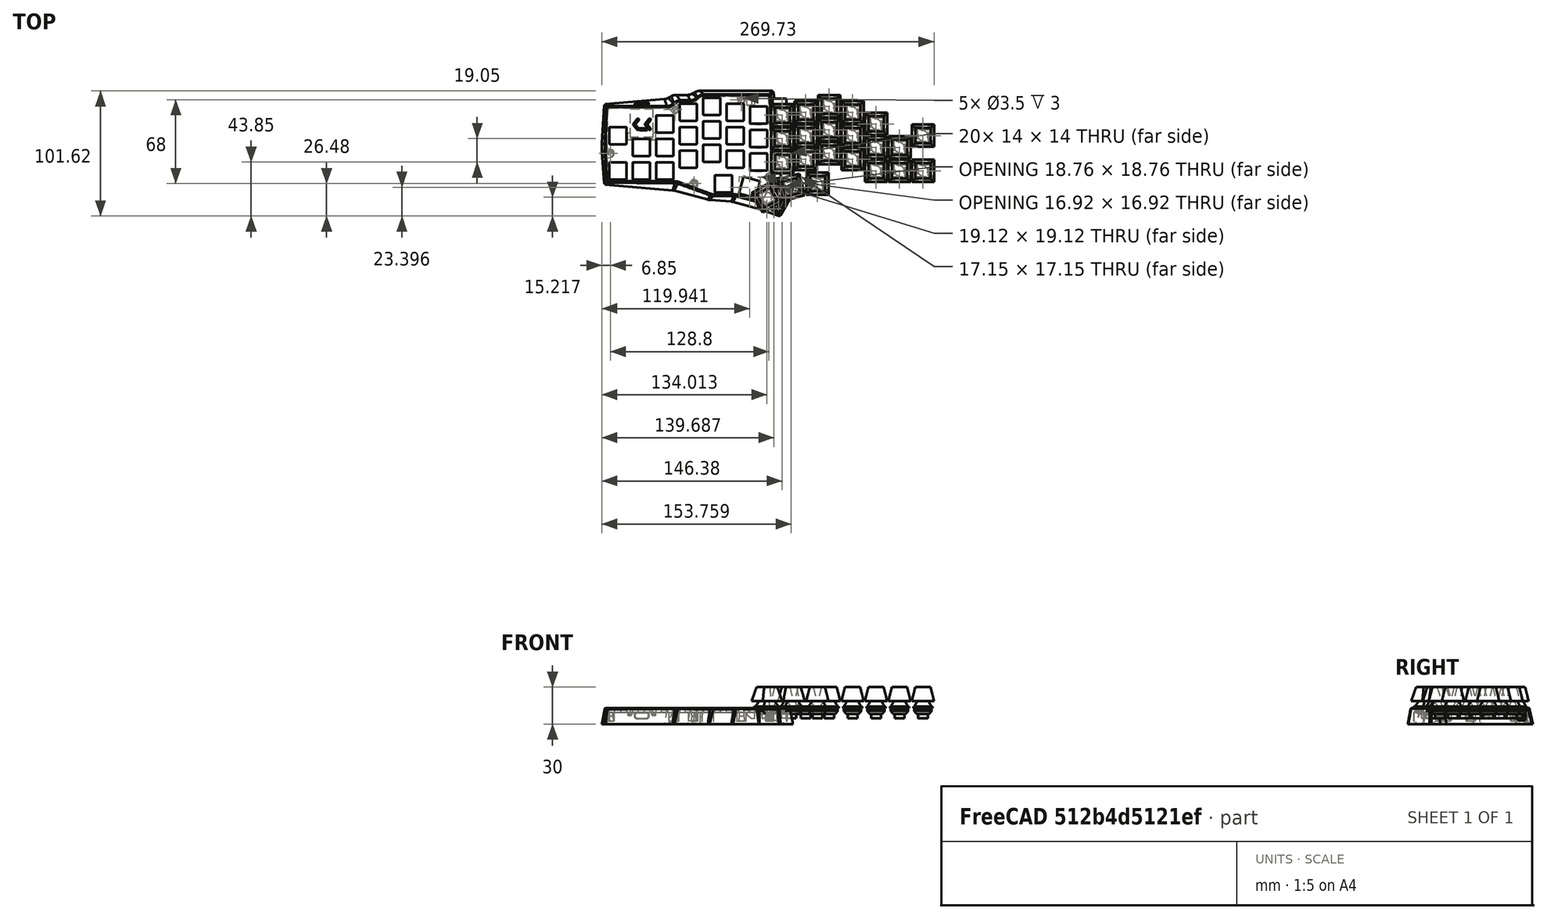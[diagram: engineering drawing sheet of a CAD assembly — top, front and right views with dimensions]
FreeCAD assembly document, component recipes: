
FREECAD ASSEMBLY — COMPONENT RECIPES ("plate6")

This assembly document has 8 components, labeled P0..P7 below (a component is one placed body or linked part). 8 of them carry a construction recipe — the FreeCAD feature program that regenerates the part from scratch, quoted from this document or its linked companion documents; the rest are supplied as boundary geometry only. No exploded tour is included for this assembly.
COMPONENT P0 — recipe-attached ("CaseSolid", modeled in this document).
Construction recipe (the document's own serialized feature program — sketch geometry with constraints, then the solid features built on it; lengths are millimeters unless a unit is written):

FEATURE [PartDesign::ShapeBinder] ShapeBinder
  Support = -> [Compound]
  TraceSupport = false
FEATURE [Sketcher::SketchObject] Sketch  label="SketchTop"
  ExternalGeometry = -> [ShapeBinder]
  FullyConstrained = true
  MapMode = 5
  Support = -> [XY_Plane]
  sketch-geometry (19):
    g0: LineSegment StartX=57.15 StartY=7.14375 StartZ=0 EndX=61.9125 EndY=2.38125 EndZ=0
    g1: LineSegment StartX=61.9125 StartY=2.38125 StartZ=0 EndX=76.2 EndY=2.38125 EndZ=0
    g2: LineSegment StartX=76.2 StartY=2.38125 StartZ=0 EndX=80.9625 EndY=-2.38124 EndZ=0
    g3: LineSegment StartX=80.9625 StartY=-2.38124 StartZ=0 EndX=133.35 EndY=-2.38124 EndZ=0
    g4: LineSegment StartX=133.35 StartY=-2.38124 StartZ=0 EndX=134.35 EndY=-33.2188 EndZ=0
    g5: LineSegment StartX=134.35 StartY=-38.2188 StartZ=0 EndX=133.35 EndY=-64.2937 EndZ=0
    g6: LineSegment StartX=133.35 StartY=-64.2937 StartZ=0 EndX=76.2 EndY=-64.2937 EndZ=0
    g7: LineSegment StartX=76.2 StartY=-64.2937 StartZ=0 EndX=47.625 EndY=-74.8187 EndZ=0
    g8: LineSegment StartX=47.625 StartY=-74.8187 StartZ=0 EndX=28.575 EndY=-74.8187 EndZ=0
    g9: LineSegment StartX=28.575 StartY=-74.8187 StartZ=0 EndX=10.1741 EndY=-79.7492 EndZ=0
    g10: LineSegment StartX=10.1741 StartY=-79.7492 StartZ=0 EndX=-6.75668 EndY=-89.5242 EndZ=0
    g11: LineSegment StartX=-16.2817 StartY=-73.0265 StartZ=0 EndX=-3.16979 EndY=-65.4563 EndZ=0
    g12: LineSegment StartX=-3.16979 StartY=-65.4563 StartZ=0 EndX=-4e-16 EndY=7.14375 EndZ=0
    g13: LineSegment StartX=-4e-16 StartY=7.14375 StartZ=0 EndX=57.15 EndY=7.14375 EndZ=0
    g14: LineSegment StartX=134.35 StartY=-33.2188 StartZ=0 EndX=134.35 EndY=-35.7188 EndZ=0
    g15: LineSegment StartX=134.35 StartY=-35.7188 StartZ=0 EndX=134.35 EndY=-38.2188 EndZ=0
    g16: GeomPoint X=133.35 Y=-7.14393 Z=0
    g17: GeomPoint X=133.35 Y=-35.7188 Z=0
    g18: LineSegment StartX=-16.2817 StartY=-73.0265 StartZ=0 EndX=-6.75668 EndY=-89.5242 EndZ=0
  constraints (47):
    c: Coincident(g0,g1)
    c: Horizontal(g1)
    c: Coincident(g1,g2)
    c: Coincident(g2,g3)
    c: Horizontal(g3)
    c: Coincident(g3,g4)
    c: Coincident(g5,g6)
    c: Horizontal(g6)
    c: Coincident(g6,g7)
    c: Coincident(g7,g8)
    c: Coincident(g8,g9)
    c: Coincident(g9,g10)
    c: Coincident(g11,g12)
    c: Coincident(g12,g13)
    c: Horizontal(g13)
    c: Coincident(g13,g0)
    c: Coincident(g-4,g0)
    c: Coincident(g1,g-5)
    c: Angle(g13,g0) = 2.35619
    c: Equal(g0,g2)
    c: Angle(g1,g2) = 2.35619
    c: Vertical(g-1,g12)
    c: Angle(g12,g13) = 1.61443
    c: Parallel(g-12,g11)
    c: Coincident(g9,g-13)
    c: Coincident(g-14,g8)
    c: Coincident(g7,g-14)
    c: Coincident(g5,g-8)
    c: Coincident(g4,g14)
    c: Vertical(g14)
    c: Coincident(g14,g15)
    c: Coincident(g15,g5)
    c: Vertical(g15)
    c: Equal(g15,g14)
    c: Coincident(g16,g-7)
    c: Symmetric(g16,g5,g17)
    c: Horizontal(g17,g14)
    c: DistanceX(g17,g14) = 1
    c: DistanceY(g14,g14) = 2.5
    c: Vertical(g3,g5)
    c: Vertical(g-9,g6)
    c: Parallel(g-10,g10)
    c: Coincident(g18,g11)
    c: Coincident(g18,g10)
    c: Parallel(g18,g-11)
    c: Distance(g-12,g18) = 0.5
    c: PointOnObject(g11,g-12)
FEATURE [Sketcher::SketchObject] Sketch001  label="SketchBot"
  AttachmentOffset = pos=(0,0,-13) rot=(0,0,1;0rad)
  ExternalGeometry = -> [ShapeBinder]
  FullyConstrained = true
  MapMode = 5
  Placement = pos=(0,0,-13) rot=(0,0,1;0rad)
  Support = -> [XY_Plane]
  expr: .AttachmentOffset.Base.z = 0 mm - <<S>>.caseHeight
  sketch-geometry (18):
    g0: LineSegment StartX=59.65 StartY=10.1437 StartZ=0 EndX=65.3008 EndY=6.88125 EndZ=0
    g1: LineSegment StartX=65.3008 StartY=6.88125 StartZ=0 EndX=78.7 EndY=6.88125 EndZ=0
    g2: LineSegment StartX=78.7 StartY=6.88125 StartZ=0 EndX=84.3508 EndY=3.61876 EndZ=0
    g3: LineSegment StartX=84.3508 StartY=3.61876 StartZ=0 EndX=134.929 EndY=-0.806253 EndZ=0
    g4: LineSegment StartX=134.929 StartY=-0.806253 StartZ=0 EndX=136.85 EndY=-32.2188 EndZ=0
    g5: LineSegment StartX=136.85 StartY=-32.2188 StartZ=0 EndX=136.85 EndY=-35.7188 EndZ=0
    g6: LineSegment StartX=136.85 StartY=-35.7188 StartZ=0 EndX=136.85 EndY=-39.2188 EndZ=0
    g7: LineSegment StartX=136.85 StartY=-39.2188 StartZ=0 EndX=134.929 EndY=-65.7937 EndZ=0
    g8: LineSegment StartX=78.7 StartY=-70.7131 StartZ=0 EndX=50.125 EndY=-78.3698 EndZ=0
    g9: LineSegment StartX=50.125 StartY=-78.3698 StartZ=0 EndX=31.075 EndY=-79.7992 EndZ=0
    g10: LineSegment StartX=31.075 StartY=-79.7992 StartZ=0 EndX=9.17411 EndY=-85.6675 EndZ=0
    g11: LineSegment StartX=9.17411 StartY=-85.6675 StartZ=0 EndX=-7.73873 EndY=-91.8233 EndZ=0
    g12: LineSegment StartX=-7.73873 StartY=-91.8233 StartZ=0 EndX=-18.7637 EndY=-72.7274 EndZ=0
    g13: LineSegment StartX=-18.7637 StartY=-72.7274 StartZ=0 EndX=-8.88611 EndY=-62.8498 EndZ=0
    g14: LineSegment StartX=-8.88611 StartY=-62.8498 StartZ=0 EndX=-2.5 EndY=10.1437 EndZ=0
    g15: LineSegment StartX=-2.5 StartY=10.1437 StartZ=0 EndX=59.65 EndY=10.1437 EndZ=0
    g16: GeomPoint X=133.35 Y=-35.7188 Z=0
    g17: LineSegment StartX=78.7 StartY=-70.7131 StartZ=0 EndX=134.929 EndY=-65.7937 EndZ=0
  constraints (52):
    c: Coincident(g0,g1)
    c: Horizontal(g1)
    c: Coincident(g1,g2)
    c: Coincident(g2,g3)
    c: Coincident(g3,g4)
    c: Coincident(g4,g5)
    c: Coincident(g5,g6)
    c: Coincident(g6,g7)
    c: Coincident(g8,g9)
    c: Coincident(g9,g10)
    c: Coincident(g10,g11)
    c: Coincident(g11,g12)
    c: Coincident(g12,g13)
    c: Coincident(g13,g14)
    c: Coincident(g14,g15)
    c: Horizontal(g15)
    c: DistanceY(g-4,g15) = 3
    c: DistanceX(g-4,g15) = 2.5
    c: Coincident(g0,g15)
    c: DistanceY(g-5,g1) = 4.5
    c: DistanceX(g-5,g1) = 2.5
    c: Angle(g15,g0) = 2.61799
    c: Equal(g0,g2)
    c: Angle(g1,g2) = 2.61799
    c: Vertical(g5)
    c: Vertical(g6)
    c: Symmetric(g-7,g-8,g16)
    c: Horizontal(g16,g5)
    c: DistanceX(g16,g5) = 3.5
    c: DistanceY(g5,g5) = 3.5
    c: Equal(g5,g6)
    c: Vertical(g7,g3)
    c: Parallel(g12,g-11)
    c: Angle(g12,g13) = 1.8326
    c: Angle(g11,g12) = 1.74533
    c: Distance(g-11,g12) = 2.5
    c: Distance(g12,g-10) = 1.5
    c: Distance(g11,g-12) = 1.5
    c: Angle(g14,g15) = 1.65806
    c: DistanceX(g14,g-1) = 2.5
    c: DistanceY(g7,g-8) = 1.5
    c: DistanceX(g-9,g8) = 2.5
    c: Parallel(g-13,g10)
    c: DistanceX(g-14,g8) = 2.5
    c: DistanceX(g-14,g9) = 2.5
    c: DistanceX(g10,g-13) = 1
    c: Angle(g-2,g4) = 0.0610865
    c: Angle(g-1,g3) = 3.05433
    c: Coincident(g17,g8)
    c: Coincident(g17,g7)
    c: Angle(g-1,g17) = 0.0872665
    c: Angle(g8,g17) = 2.96706
FEATURE [Sketcher::SketchObject] Sketch002
  AttachmentOffset = pos=(0,0,-3.6) rot=(0,0,1;0rad)
  ExternalGeometry = -> [Sketch]
  FullyConstrained = false
  MapMode = 5
  Placement = pos=(0,0,-3.6) rot=(0,0,1;0rad)
  Support = -> [XY_Plane]
  expr: .AttachmentOffset.Base.z = -<<S>>.topThk
  sketch-geometry (17):
    g0: LineSegment StartX=1.43594 StartY=5.64375 StartZ=0 EndX=56.5287 EndY=5.64375 EndZ=0
    g1: LineSegment StartX=56.5287 StartY=5.64375 StartZ=0 EndX=61.2912 EndY=0.881255 EndZ=0
    g2: LineSegment StartX=61.2912 StartY=0.881255 StartZ=0 EndX=75.5787 EndY=0.881255 EndZ=0
    g3: LineSegment StartX=75.5787 StartY=0.881255 StartZ=0 EndX=80.3412 EndY=-3.88124 EndZ=0
    g4: LineSegment StartX=80.3412 StartY=-3.88124 StartZ=0 EndX=131.898 EndY=-3.88124 EndZ=0
    g5: LineSegment StartX=131.898 StartY=-3.88124 StartZ=0 EndX=132.851 EndY=-33.2719 EndZ=0
    g6: LineSegment StartX=132.851 StartY=-33.2719 StartZ=0 EndX=132.851 EndY=-35.7188 EndZ=0
    g7: LineSegment StartX=132.851 StartY=-35.7188 StartZ=0 EndX=132.851 EndY=-38.1658 EndZ=0
    g8: LineSegment StartX=132.851 StartY=-38.1658 StartZ=0 EndX=131.906 EndY=-62.7937 EndZ=0
    g9: LineSegment StartX=131.906 StartY=-62.7937 StartZ=0 EndX=75.9325 EndY=-62.7937 EndZ=0
    g10: LineSegment StartX=75.9325 StartY=-62.7937 StartZ=0 EndX=47.3575 EndY=-73.3187 EndZ=0
    g11: LineSegment StartX=47.3575 StartY=-73.3187 StartZ=0 EndX=28.3775 EndY=-73.3187 EndZ=0
    g12: LineSegment StartX=28.3775 StartY=-73.3187 StartZ=0 EndX=9.59513 EndY=-78.3515 EndZ=0
    g13: LineSegment StartX=9.59513 StartY=-78.3515 StartZ=0 EndX=-5.77463 EndY=-87.2252 EndZ=0
    g14: LineSegment StartX=-5.77463 StartY=-87.2252 StartZ=0 EndX=-13.7996 EndY=-73.3255 EndZ=0
    g15: LineSegment StartX=-13.7996 StartY=-73.3255 StartZ=0 EndX=-1.70711 EndY=-66.3439 EndZ=0
    g16: LineSegment StartX=-1.70711 StartY=-66.3439 StartZ=0 EndX=1.43594 EndY=5.64375 EndZ=0
  constraints (24):
    c: Horizontal(g0)
    c: Coincident(g0,g1)
    c: Coincident(g1,g2)
    c: Horizontal(g2)
    c: Coincident(g2,g3)
    c: Coincident(g3,g4)
    c: Horizontal(g4)
    c: Coincident(g4,g5)
    c: Coincident(g5,g6)
    c: Vertical(g6)
    c: Coincident(g6,g7)
    c: Vertical(g7)
    c: Coincident(g7,g8)
    c: Coincident(g8,g9)
    c: Horizontal(g9)
    c: Coincident(g9,g10)
    c: Coincident(g10,g11)
    c: Coincident(g11,g12)
    c: Coincident(g12,g13)
    c: Coincident(g13,g14)
    c: Coincident(g14,g15)
    c: Coincident(g15,g16)
    c: Coincident(g16,g0)
    c: Equal(g6,g7)
FEATURE [Sketcher::SketchObject] Sketch003
  AttachmentOffset = pos=(0,0,-3) rot=(0,0,1;0rad)
  FullyConstrained = true
  MapMode = 5
  Placement = pos=(0,0,-3) rot=(0,0,1;0rad)
  Support = -> [XY_Plane]
  expr: .AttachmentOffset.Base.z = -3
  sketch-geometry (12):
    g0: LineSegment StartX=115.875 StartY=-23.625 StartZ=0 EndX=113.875 EndY=-23.625 EndZ=0
    g1: LineSegment StartX=113.875 StartY=-23.625 StartZ=0 EndX=113.875 EndY=-27.625 EndZ=0
    g2: LineSegment StartX=113.875 StartY=-27.625 StartZ=0 EndX=112.375 EndY=-27.625 EndZ=0
    g3: LineSegment StartX=112.375 StartY=-27.625 StartZ=0 EndX=112.375 EndY=-29.625 EndZ=0
    g4: LineSegment StartX=112.375 StartY=-29.625 StartZ=0 EndX=115.875 EndY=-29.625 EndZ=0
    g5: LineSegment StartX=115.875 StartY=-29.625 StartZ=0 EndX=115.875 EndY=-23.625 EndZ=0
    g6: LineSegment StartX=95.275 StartY=-23.625 StartZ=0 EndX=93.275 EndY=-23.625 EndZ=0
    g7: LineSegment StartX=93.275 StartY=-23.625 StartZ=0 EndX=93.275 EndY=-29.625 EndZ=0
    g8: LineSegment StartX=93.275 StartY=-29.625 StartZ=0 EndX=96.775 EndY=-29.625 EndZ=0
    g9: LineSegment StartX=96.775 StartY=-29.625 StartZ=0 EndX=96.775 EndY=-27.625 EndZ=0
    g10: LineSegment StartX=96.775 StartY=-27.625 StartZ=0 EndX=95.275 EndY=-27.625 EndZ=0
    g11: LineSegment StartX=95.275 StartY=-27.625 StartZ=0 EndX=95.275 EndY=-23.625 EndZ=0
  constraints (36):
    c: Horizontal(g0)
    c: Coincident(g0,g1)
    c: Coincident(g1,g2)
    c: Coincident(g2,g3)
    c: Coincident(g3,g4)
    c: Horizontal(g4)
    c: Coincident(g4,g5)
    c: Vertical(g5)
    c: Coincident(g0,g5)
    c: Vertical(g1)
    c: Horizontal(g2)
    c: Vertical(g3)
    c: DistanceY(g3,g3) = 2
    c: DistanceX(g1) = 113.875
    c: DistanceY(g1) = -27.625
    c: DistanceX(g0,g0) = 2
    c: DistanceY(g5,g5) = 6
    c: DistanceX(g4,g4) = 3.5
    c: Horizontal(g6)
    c: Coincident(g6,g7)
    c: Vertical(g7)
    c: Coincident(g7,g8)
    c: Coincident(g8,g9)
    c: Vertical(g9)
    c: Coincident(g9,g10)
    c: Coincident(g10,g11)
    c: Coincident(g11,g6)
    c: Vertical(g11)
    c: Horizontal(g10)
    c: Horizontal(g8)
    c: Equal(g3,g9)
    c: Equal(g6,g0)
    c: Horizontal(g0,g6)
    c: Horizontal(g3,g8)
    c: Equal(g8,g4)
    c: DistanceX(g8,g3) = 15.6
FEATURE [PartDesign::FeatureBase] BaseFeature
  BaseFeature = -> Compound004
FEATURE [PartDesign::AdditiveLoft] AdditiveLoft
  BaseFeature = -> BaseFeature
  Closed = false
  Profile = -> Sketch
  Ruled = false
  Sections = -> [Sketch001]
FEATURE [PartDesign::Pocket] Pocket
  BaseFeature = -> AdditiveLoft
  Direction = (0,0,-1)
  Length = 5
  Length2 = 5
  Profile = -> Sketch002
  ReferenceAxis = -> Sketch002 [N_Axis]
  Refine = true
  Type = 1
FEATURE [PartDesign::Chamfer] Chamfer
  Angle = 45
  Base = -> Pocket [Edge21,Edge31,Edge39,Edge49,Edge20]
  BaseFeature = -> Pocket
  ChamferType = 0
  FlipDirection = false
  Size = 1
  Size2 = 1
  SupportTransform = false
  UseAllEdges = false
FEATURE [PartDesign::Fillet] Fillet
  Base = -> Chamfer [Edge36,Edge40,Edge44,Edge48,Edge60,Edge62,Edge51,Edge47,Edge43,Edge38,Edge24]
  BaseFeature = -> Chamfer
  Radius = 8
  SupportTransform = false
  UseAllEdges = false
FEATURE [PartDesign::Chamfer] Chamfer001
  Angle = 45
  Base = -> Fillet [Edge142,Edge118,Edge117,Edge120,Edge122,Edge124,Edge130,Edge126,Edge128,Edge132,Edge134,Edge136,Edge140,Edge138]
  BaseFeature = -> Fillet
  ChamferType = 0
  FlipDirection = false
  Size = 1
  Size2 = 1
  SupportTransform = false
  UseAllEdges = false
FEATURE [PartDesign::Pad] Pad
  BaseFeature = -> Chamfer001
  Direction = (0,0,1)
  Length = 3
  Length2 = 10
  Profile = -> Sketch003
  ReferenceAxis = -> Sketch003 [N_Axis]
  Reversed = true
  Type = 0
FEATURE [Sketcher::SketchObject] Sketch004
  FullyConstrained = true
  MapMode = 5
  Placement = pos=(0,0,-3.6) rot=(1,0,0;3.14159rad)
  Support = -> [Pad]
  expr: Constraints[8] = <<S>>.trsOffset
  sketch-geometry (6):
    g0: LineSegment StartX=13 StartY=1.5 StartZ=0 EndX=19 EndY=1.5 EndZ=0
    g1: LineSegment StartX=19 StartY=1.5 StartZ=0 EndX=19 EndY=-4 EndZ=0
    g2: LineSegment StartX=19 StartY=-4 StartZ=0 EndX=13 EndY=-4 EndZ=0
    g3: LineSegment StartX=13 StartY=-4 StartZ=0 EndX=13 EndY=1.5 EndZ=0
    g4: GeomPoint X=1.54 Y=-4 Z=0
    g5: LineSegment StartX=13 StartY=-4 StartZ=0 EndX=1.54 EndY=-4 EndZ=0
  constraints (17):
    c: Coincident(g0,g1)
    c: Coincident(g1,g2)
    c: Coincident(g2,g3)
    c: Coincident(g3,g0)
    c: Horizontal(g0)
    c: Horizontal(g2)
    c: Vertical(g1)
    c: Vertical(g3)
    c: DistanceX(g0) = 13
    c: DistanceY(g0) = 1.5
    c: DistanceX(g0,g0) = 6
    c: DistanceY(g1,g1) = 5.5
    c: DistanceX(g-1,g4) = 1.54
    c: Horizontal(g4,g2)
    c: Coincident(g5,g2)
    c: Coincident(g4,g5)
    c: DistanceX(g5,g5) = 11.46
FEATURE [PartDesign::Pad] Pad001
  BaseFeature = -> Pad
  Direction = (0,0,-1)
  Length = 5
  Length2 = 10
  Profile = -> Sketch004
  ReferenceAxis = -> Sketch004 [N_Axis]
  Type = 0
FEATURE [PartDesign::Chamfer] Chamfer002
  Angle = 45
  Base = -> Pad001 [Edge234]
  BaseFeature = -> Pad001
  ChamferType = 1
  FlipDirection = false
  Size = 3
  Size2 = 4
  SupportTransform = false
  UseAllEdges = false
FEATURE [PartDesign::Chamfer] Chamfer006
  Angle = 45
  Base = -> Chamfer002 [Edge141,Edge132,Edge129,Edge120]
  BaseFeature = -> Chamfer002
  ChamferType = 0
  FlipDirection = false
  Size = 1
  Size2 = 1
  SupportTransform = false
  UseAllEdges = false
FEATURE [PartDesign::Body] Body  label="CaseSolid"
  BaseFeature = -> Compound004
  Group = -> [BaseFeature,ShapeBinder,Sketch,Sketch001,AdditiveLoft,Sketch002,Pocket,Chamfer,Fillet,Chamfer001,Sketch003,Pad,Sketch004,Pad001,Chamfer002,Chamfer006]
  Origin = -> Origin
  Tip = -> Chamfer006
COMPONENT P1 — recipe-attached ("USBC-Cutout", modeled in this document).
Construction recipe (the document's own serialized feature program — sketch geometry with constraints, then the solid features built on it; lengths are millimeters unless a unit is written):

FEATURE [Sketcher::SketchObject] Sketch005
  FullyConstrained = true
  MapMode = 5
  Placement = pos=(0,0,0) rot=(1,0,0;1.5708rad)
  Support = -> [XZ_Plane002]
  expr: Constraints[16] = 4.6 mm + 0.1 mm + 0.1 mm
  expr: Constraints[17] = 10.5 mm + 0.1 mm + 0.1 mm
  expr: Constraints[20] = <<S>>.usbcCutoutOffset
  sketch-geometry (9):
    g0: LineSegment StartX=107.85 StartY=-3.8 StartZ=0 EndX=101.15 EndY=-3.8 EndZ=0
    g1: LineSegment StartX=99.15 StartY=-5.8 StartZ=0 EndX=99.15 EndY=-6.6 EndZ=0
    g2: LineSegment StartX=101.15 StartY=-8.6 StartZ=0 EndX=107.85 EndY=-8.6 EndZ=0
    g3: LineSegment StartX=109.85 StartY=-6.6 StartZ=0 EndX=109.85 EndY=-5.8 EndZ=0
    g4: ArcOfCircle CenterX=107.85 CenterY=-5.8 CenterZ=0 NormalX=0 NormalY=0 NormalZ=1 AngleXU=0 Radius=2 StartAngle=0 EndAngle=1.5708
    g5: ArcOfCircle CenterX=101.15 CenterY=-5.8 CenterZ=0 NormalX=0 NormalY=0 NormalZ=1 AngleXU=0 Radius=2 StartAngle=1.5708 EndAngle=3.14159
    g6: ArcOfCircle CenterX=107.85 CenterY=-6.6 CenterZ=0 NormalX=0 NormalY=0 NormalZ=1 AngleXU=0 Radius=2 StartAngle=4.71239 EndAngle=6.28319
    g7: ArcOfCircle CenterX=101.15 CenterY=-6.6 CenterZ=0 NormalX=0 NormalY=0 NormalZ=1 AngleXU=0 Radius=2 StartAngle=3.14159 EndAngle=4.71239
    g8: GeomPoint X=104.5 Y=-6.2 Z=0
  constraints (21):
    c: Horizontal(g0)
    c: Horizontal(g2)
    c: Vertical(g1)
    c: Vertical(g3)
    c: Tangent(g3,g4) = -1.5708
    c: Tangent(g0,g4) = -1.5708
    c: Tangent(g0,g5) = -1.5708
    c: Tangent(g1,g5) = -1.5708
    c: Tangent(g3,g6) = -1.5708
    c: Tangent(g2,g6) = -1.5708
    c: Tangent(g2,g7) = -1.5708
    c: Tangent(g1,g7) = -1.5708
    c: Radius(g4) = 2
    c: Equal(g4,g5)
    c: Equal(g5,g7)
    c: Equal(g7,g6)
    c: DistanceY(g2,g0) = 4.8
    c: DistanceX(g1,g3) = 10.7
    c: Symmetric(g0,g2,g8)
    c: DistanceX(g-1,g8) = 104.5
    c: DistanceY(g8,g-1) = 6.2
FEATURE [PartDesign::Pad] Pad002
  Direction = (0,-1,-2e-16)
  Length = 8
  Length2 = 10
  Midplane = true
  Placement = pos=(0,0,0) rot=(1,0,0;1.5708rad)
  Profile = -> Sketch005
  ReferenceAxis = -> Sketch005 [N_Axis]
  Type = 0
FEATURE [PartDesign::Body] Body002  label="USBC-Cutout"
  Group = -> [Sketch005,Pad002]
  Origin = -> Origin002
  Tip = -> Pad002
COMPONENT P2 — recipe-attached ("TRRS-Cutout", modeled in this document).
Construction recipe (the document's own serialized feature program — sketch geometry with constraints, then the solid features built on it; lengths are millimeters unless a unit is written):

FEATURE [Sketcher::SketchObject] Sketch006
  FullyConstrained = true
  MapMode = 5
  Placement = pos=(0,0,0) rot=(0.57735,0.57735,0.57735;2.0944rad)
  Support = -> [YZ_Plane003]
  expr: Constraints[2] = 2.5 mm + 0.1 mm + 0.1 mm
  sketch-geometry (1):
    g0: Circle CenterX=1.125 CenterY=-6.5 CenterZ=0 NormalX=0 NormalY=0 NormalZ=1 AngleXU=0 Radius=2.7
  constraints (3):
    c: DistanceX(g0) = 1.125
    c: DistanceY(g0) = -6.5
    c: Radius(g0) = 2.7
FEATURE [PartDesign::Pad] Pad003
  Direction = (1,-2e-16,3e-16)
  Length = 20
  Length2 = 10
  Midplane = true
  Placement = pos=(0,0,0) rot=(0.57735,0.57735,0.57735;2.0944rad)
  Profile = -> Sketch006
  ReferenceAxis = -> Sketch006 [N_Axis]
  Type = 0
FEATURE [PartDesign::Body] Body003  label="TRRS-Cutout"
  Group = -> [Sketch006,Pad003]
  Origin = -> Origin003
  Tip = -> Pad003
COMPONENT P3 — recipe-attached ("MCU-Cutout", modeled in this document).
Construction recipe (the document's own serialized feature program — sketch geometry with constraints, then the solid features built on it; lengths are millimeters unless a unit is written):

FEATURE [Sketcher::SketchObject] Sketch007
  FullyConstrained = false
  MapMode = 5
  Support = -> [XY_Plane004]
  sketch-geometry (6):
    g0: LineSegment StartX=113.7 StartY=-27.5 StartZ=0 EndX=95.5 EndY=-27.5 EndZ=0
    g1: LineSegment StartX=95.5 StartY=-27.5 StartZ=0 EndX=95.5 EndY=-4.3 EndZ=0
    g2: LineSegment StartX=95.5 StartY=-4.3 StartZ=0 EndX=113.7 EndY=-4.3 EndZ=0
    g3: LineSegment StartX=113.7 StartY=-4.3 StartZ=0 EndX=113.7 EndY=-27.5 EndZ=0
    g4: GeomPoint X=104.6 Y=-15.9 Z=0
    g5: GeomPoint X=104.6 Y=-27.6247 Z=0
  constraints (14):
    c: Coincident(g0,g1)
    c: Coincident(g1,g2)
    c: Coincident(g2,g3)
    c: Coincident(g3,g0)
    c: Horizontal(g0)
    c: Horizontal(g2)
    c: Vertical(g1)
    c: Vertical(g3)
    c: Symmetric(g0,g2,g4)
    c: DistanceX(g0,g0) = 18.2
    c: Vertical(g5,g4)
    c: DistanceX(g4) = 104.6
    c: DistanceY(g4) = -15.9
    c: DistanceY(g3,g3) = 23.2
FEATURE [PartDesign::Pad] Pad004
  Direction = (0,0,1)
  Length = 3
  Length2 = 10
  Profile = -> Sketch007
  ReferenceAxis = -> Sketch007 [N_Axis]
  Type = 0
FEATURE [PartDesign::Body] Body004  label="MCU-Cutout"
  Group = -> [Sketch007,Pad004]
  Origin = -> Origin004
  Placement = pos=(0,0,-4.5) rot=(0,0,1;0rad)
  Tip = -> Pad004
COMPONENT P4 — recipe-attached ("HeatsetHolderR", a linked part whose construction recipe lives in a companion FreeCAD document of the same project; that document's serialized recipe follows).
Construction recipe (the companion document, serialized — sketch geometry with constraints, then the solid features built on it; lengths are millimeters unless a unit is written):

FCSTD DOCUMENT  (FreeCAD 0.21R33668 +26 (Git))
Label: HeatSetInsertHolder
License: All rights reserved
LicenseURL: http://en.wikipedia.org/wiki/All_rights_reserved
objects: Sketcher::SketchObject×1, PartDesign::Pad×1, PartDesign::Body×1, Part::Refine×1
note: 5 computed .brp shape members not serialized (recipe doc carries the construction recipe); baked Part::Feature solids carry a one-line shape summary decoded from their .brp

FEATURE [Sketcher::SketchObject] Sketch018
  AttachmentOffset = pos=(0,0,-1) rot=(0,0,1;0rad)
  FullyConstrained = true
  MapMode = 5
  Placement = pos=(0,0,-1) rot=(0,0,1;0rad)
  Support = -> [XY_Plane009]
  sketch-geometry (9):
    g0: LineSegment StartX=-4 StartY=3.8589 StartZ=0 EndX=4 EndY=3.8589 EndZ=0
    g1: LineSegment StartX=4 StartY=3.8589 StartZ=0 EndX=2.94356 EndY=-1.02822 EndZ=0
    g2: LineSegment StartX=0.5 StartY=-3 StartZ=0 EndX=-0.5 EndY=-3 EndZ=0
    g3: LineSegment StartX=-2.94356 StartY=-1.02822 StartZ=0 EndX=-4 EndY=3.8589 EndZ=0
    g4: ArcOfCircle CenterX=-0.5 CenterY=-0.5 CenterZ=0 NormalX=0 NormalY=0 NormalZ=1 AngleXU=0 Radius=2.5 StartAngle=3.35449 EndAngle=4.71239
    g5: ArcOfCircle CenterX=0.5 CenterY=-0.5 CenterZ=0 NormalX=0 NormalY=0 NormalZ=1 AngleXU=0 Radius=2.5 StartAngle=4.71239 EndAngle=6.07029
    g6: GeomPoint X=0 Y=0 Z=0
    g7: LineSegment StartX=-0.5 StartY=-0.5 StartZ=0 EndX=0 EndY=0 EndZ=0
    g8: LineSegment StartX=0 StartY=0 StartZ=0 EndX=0.5 EndY=-0.5 EndZ=0
  constraints (21):
    c: Coincident(g0,g1)
    c: Coincident(g3,g0)
    c: Horizontal(g0)
    c: Horizontal(g2)
    c: Tangent(g3,g4) = 1.5708
    c: Tangent(g2,g4) = 1.5708
    c: Tangent(g2,g5) = 1.5708
    c: Tangent(g1,g5) = 1.5708
    c: Equal(g4,g5)
    c: Equal(g1,g3)
    c: Radius(g4) = 2.5
    c: DistanceX(g2,g2) = 1
    c: DistanceX(g0,g0) = 8
    c: Distance(g1) = 5
    c: Coincident(g7,g4)
    c: Coincident(g7,g6)
    c: Coincident(g8,g7)
    c: Coincident(g8,g5)
    c: Equal(g8,g7)
    c: DistanceY(g5,g7) = 0.5
    c: Coincident(g6,g-1)
FEATURE [PartDesign::Pad] Pad009
  Direction = (0,0,1)
  Length = 9.5
  Length2 = 10
  Profile = -> Sketch018
  ReferenceAxis = -> Sketch018 [N_Axis]
  Reversed = true
  Type = 0
  expr: Length = 12 mm - 1.5 mm - 1 mm
FEATURE [PartDesign::Body] Body009  label="HeatsetHolder"
  Group = -> [Sketch018,Pad009]
  Origin = -> Origin009
  Tip = -> Pad009
FEATURE [Part::Refine] Body010  label="HeatsetHolderR"
  Source = -> Body009
COMPONENT P5 — recipe-attached ("ScrewAndInsertR", a linked part whose construction recipe lives in a companion FreeCAD document of the same project; that document's serialized recipe follows).
Construction recipe (the companion document, serialized — sketch geometry with constraints, then the solid features built on it; lengths are millimeters unless a unit is written):

FCSTD DOCUMENT  (FreeCAD 0.21R33668 +26 (Git))
Label: ScrewAndInsertCutout
License: All rights reserved
LicenseURL: http://en.wikipedia.org/wiki/All_rights_reserved
objects: Sketcher::SketchObject×4, PartDesign::Pad×2, PartDesign::AdditiveLoft×1, PartDesign::Body×1, Part::Refine×1, Spreadsheet::Sheet×1
note: 12 computed .brp shape members not serialized (recipe doc carries the construction recipe); baked Part::Feature solids carry a one-line shape summary decoded from their .brp

FEATURE [Sketcher::SketchObject] Sketch014
  AttachmentOffset = pos=(0,0,-5) rot=(0,0,1;0rad)
  FullyConstrained = true
  MapMode = 5
  Placement = pos=(0,0,-5) rot=(0,0,1;0rad)
  Support = -> [XY_Plane008]
  expr: Constraints[1] = <<S>>.hsDia
  sketch-geometry (1):
    g0: Circle CenterX=0 CenterY=0 CenterZ=0 NormalX=0 NormalY=0 NormalZ=1 AngleXU=0 Radius=1.75
  constraints (2):
    c: Coincident(g0,g-1)
    c: Diameter(g0) = 3.5
FEATURE [Sketcher::SketchObject] Sketch015
  AttachmentOffset = pos=(0,0,-5) rot=(0,0,1;0rad)
  FullyConstrained = true
  MapMode = 5
  Placement = pos=(0,0,-5) rot=(0,0,1;0rad)
  Support = -> [XY_Plane008]
  expr: .AttachmentOffset.Base.z = <<S>>.hsHei
  expr: Constraints[1] = <<S>>.hsDia
  sketch-geometry (1):
    g0: Circle CenterX=0 CenterY=0 CenterZ=0 NormalX=0 NormalY=0 NormalZ=1 AngleXU=0 Radius=1.75
  constraints (2):
    c: Coincident(g0,g-1)
    c: Diameter(g0) = 3.5
FEATURE [Sketcher::SketchObject] Sketch016
  AttachmentOffset = pos=(0,0,-9) rot=(0,0,1;0rad)
  FullyConstrained = true
  MapMode = 5
  Placement = pos=(0,0,-9) rot=(0,0,1;0rad)
  Support = -> [XY_Plane008]
  expr: .AttachmentOffset.Base.z = <<S>>.hslHei
  expr: Constraints[1] = <<S>>.hslDia
  sketch-geometry (1):
    g0: Circle CenterX=0 CenterY=0 CenterZ=0 NormalX=0 NormalY=0 NormalZ=1 AngleXU=0 Radius=2.5
  constraints (2):
    c: Coincident(g0,g-1)
    c: Diameter(g0) = 5
FEATURE [PartDesign::AdditiveLoft] AdditiveLoft001  label="AdditiveLoft"
  Closed = false
  Profile = -> Sketch015
  Ruled = false
  Sections = -> [Sketch016]
FEATURE [Sketcher::SketchObject] Sketch017
  AttachmentOffset = pos=(0,0,-9) rot=(0,0,1;0rad)
  FullyConstrained = true
  MapMode = 5
  Placement = pos=(0,0,-9) rot=(0,0,1;0rad)
  Support = -> [XY_Plane008]
  expr: Constraints[1] = <<S>>.scrDia
  sketch-geometry (1):
    g0: Circle CenterX=0 CenterY=0 CenterZ=0 NormalX=0 NormalY=0 NormalZ=1 AngleXU=0 Radius=1.5
  constraints (2):
    c: Coincident(g0,g-1)
    c: Diameter(g0) = 3
FEATURE [PartDesign::Pad] Pad007
  BaseFeature = -> AdditiveLoft001
  Direction = (0,0,1)
  Length = 20
  Length2 = 10
  Profile = -> Sketch017
  ReferenceAxis = -> Sketch017 [N_Axis]
  Reversed = true
  Type = 0
  expr: Length = <<S>>.scrHei
FEATURE [PartDesign::Pad] Pad008
  BaseFeature = -> Pad007
  Direction = (0,0,1)
  Length = 3
  Length2 = 10
  Profile = -> Sketch014
  ReferenceAxis = -> Sketch014 [N_Axis]
  Type = 0
FEATURE [PartDesign::Body] Body008  label="ScrewAndInsert"
  Group = -> [Sketch014,Sketch015,Sketch016,Sketch017,AdditiveLoft001,Pad007,Pad008]
  Origin = -> Origin008
  Tip = -> Pad008
FEATURE [Part::Refine] Body009  label="ScrewAndInsertR"
  Source = -> Body008
FEATURE [Spreadsheet::Sheet] Spreadsheet  label="S"
  cells = A1='Screw Diameter; B1(scrDia)==3 mm; C1='M3 hex countersunk; D1='Screw Height; E1(scrHei)==20 mm; F1='Through all to cut through bottom plate; A2='Heatset Loft; B2(hslDia)==5 mm; D2='Loft Height; E2(hslHei)==0 mm - 9 mm; A3='HeatsetDiameter; B3(hsDia)==3.5 mm; D3='Insert Height; E3(hsHei)==0 mm - 5 mm
COMPONENT P6 — recipe-attached ("ShiftyStampR", a linked part whose construction recipe lives in a companion FreeCAD document of the same project; that document's serialized recipe follows).
Construction recipe (the companion document, serialized — sketch geometry with constraints, then the solid features built on it; lengths are millimeters unless a unit is written):

FCSTD DOCUMENT  (FreeCAD 0.21R33668 +26 (Git))
Label: Shifty
License: All rights reserved
LicenseURL: http://en.wikipedia.org/wiki/All_rights_reserved
objects: Sketcher::SketchObject×3, PartDesign::Pad×3, PartDesign::LinearPattern×1, PartDesign::Body×1, Part::Refine×1
note: 12 computed .brp shape members not serialized (recipe doc carries the construction recipe); baked Part::Feature solids carry a one-line shape summary decoded from their .brp

FEATURE [Sketcher::SketchObject] Sketch
  FullyConstrained = true
  MapMode = 5
  Support = -> [XY_Plane]
  sketch-geometry (4):
    g0: LineSegment StartX=-9.5 StartY=9.5 StartZ=0 EndX=9.5 EndY=9.5 EndZ=0
    g1: LineSegment StartX=9.5 StartY=9.5 StartZ=0 EndX=9.5 EndY=-9.5 EndZ=0
    g2: LineSegment StartX=9.5 StartY=-9.5 StartZ=0 EndX=-9.5 EndY=-9.5 EndZ=0
    g3: LineSegment StartX=-9.5 StartY=-9.5 StartZ=0 EndX=-9.5 EndY=9.5 EndZ=0
  constraints (11):
    c: Coincident(g0,g1)
    c: Coincident(g1,g2)
    c: Coincident(g2,g3)
    c: Coincident(g3,g0)
    c: Horizontal(g0)
    c: Horizontal(g2)
    c: Vertical(g1)
    c: Vertical(g3)
    c: Symmetric(g0,g1,g-1)
    c: Equal(g3,g0)
    c: DistanceX(g0,g0) = 19
FEATURE [Sketcher::SketchObject] Sketch001
  FullyConstrained = false
  MapMode = 5
  Support = -> [XY_Plane]
  sketch-geometry (18):
    g0: LineSegment StartX=-9.5 StartY=9.5 StartZ=0 EndX=9.5 EndY=9.5 EndZ=0
    g1: LineSegment StartX=9.5 StartY=9.5 StartZ=0 EndX=9.5 EndY=-9.5 EndZ=0
    g2: LineSegment StartX=9.5 StartY=-9.5 StartZ=0 EndX=-9.5 EndY=-9.5 EndZ=0
    g3: LineSegment StartX=-9.5 StartY=-9.5 StartZ=0 EndX=-9.5 EndY=9.5 EndZ=0
    g4: LineSegment StartX=-9.18334 StartY=4.33111 StartZ=0 EndX=-5.81879 EndY=0.321394 EndZ=0
    g5: LineSegment StartX=-5.81879 StartY=-0.321394 StartZ=0 EndX=-9.18334 EndY=-4.33111 EndZ=0
    g6: LineSegment StartX=-9.15387 StartY=-5.00606 StartZ=0 EndX=-8.44407 EndY=-5.71586 EndZ=0
    g7: LineSegment StartX=-7.70749 StartY=-5.6837 StartZ=0 EndX=-3.20798 EndY=-0.321394 EndZ=0
    g8: LineSegment StartX=-3.20798 StartY=0.321394 StartZ=0 EndX=-7.70749 EndY=5.6837 EndZ=0
    g9: LineSegment StartX=-8.44407 StartY=5.71586 StartZ=0 EndX=-9.15387 EndY=5.00606 EndZ=0
    g10: ArcOfCircle CenterX=-8.80032 CenterY=4.6525 CenterZ=0 NormalX=0 NormalY=0 NormalZ=1 AngleXU=0 Radius=0.5 StartAngle=2.35619 EndAngle=3.83972
    g11: ArcOfCircle CenterX=-8.09051 CenterY=5.36231 CenterZ=0 NormalX=0 NormalY=0 NormalZ=1 AngleXU=0 Radius=0.5 StartAngle=0.698132 EndAngle=2.35619
    g12: ArcOfCircle CenterX=-8.80032 CenterY=-4.6525 CenterZ=0 NormalX=0 NormalY=0 NormalZ=1 AngleXU=0 Radius=0.5 StartAngle=2.44346 EndAngle=3.92699
    g13: ArcOfCircle CenterX=-8.09051 CenterY=-5.36231 CenterZ=0 NormalX=0 NormalY=0 NormalZ=1 AngleXU=0 Radius=0.5 StartAngle=3.92699 EndAngle=5.58505
    g14: ArcOfCircle CenterX=-3.591 CenterY=-2.4e-15 CenterZ=0 NormalX=0 NormalY=0 NormalZ=1 AngleXU=0 Radius=0.5 StartAngle=5.58505 EndAngle=6.98132
    g15: GeomPoint X=-2.9383 Y=-2.7e-15 Z=0
    g16: ArcOfCircle CenterX=-6.20181 CenterY=0 CenterZ=0 NormalX=0 NormalY=0 NormalZ=1 AngleXU=0 Radius=0.5 StartAngle=5.58505 EndAngle=6.98132
    g17: GeomPoint X=-5.54911 Y=-2.7e-15 Z=0
  constraints (44):
    c: Coincident(g0,g1)
    c: Coincident(g1,g2)
    c: Coincident(g2,g3)
    c: Coincident(g3,g0)
    c: Horizontal(g0)
    c: Horizontal(g2)
    c: Vertical(g1)
    c: Vertical(g3)
    c: Symmetric(g0,g1,g-1)
    c: Equal(g3,g0)
    c: DistanceX(g0,g0) = 19
    c: Tangent(g9,g10) = -1.5708
    c: Tangent(g4,g10) = -1.5708
    c: Tangent(g9,g11) = -1.5708
    c: Tangent(g8,g11) = -1.5708
    c: Tangent(g5,g12) = -1.5708
    c: Tangent(g6,g12) = -1.5708
    c: Tangent(g7,g13) = -1.5708
    c: Tangent(g6,g13) = -1.5708
    c: Equal(g12,g13)
    c: Equal(g12,g10)
    c: Equal(g11,g10)
    c: Horizontal(g17,g15)
    c: Equal(g9,g6)
    c: Distance(g17,g7) = 2
    c: Parallel(g4,g8)
    c: Parallel(g5,g7)
    c: Angle(g-1,g9) = 0.785398
    c: Angle(g6,g-1) = 0.785398
    c: PointOnObject(g15,g8)
    c: PointOnObject(g15,g7)
    c: Tangent(g8,g14) = -1.5708
    c: Tangent(g7,g14) = -1.5708
    c: Radius(g14) = 0.5
    c: PointOnObject(g17,g4)
    c: PointOnObject(g17,g5)
    c: Tangent(g4,g16) = 1.5708
    c: Tangent(g5,g16) = 1.5708
    c: Equal(g16,g14)
    c: Equal(g4,g5)
    c: Angle(g-1,g8) = 2.26893
    c: Horizontal(g16,g-1)
    c: Radius(g11) = 0.5
    c: Distance(g8) = 7
FEATURE [PartDesign::Pad] Pad
  Direction = (0,0,1)
  Length = 25
  Length2 = 10
  Profile = -> Sketch
  ReferenceAxis = -> Sketch [N_Axis]
  Type = 0
FEATURE [PartDesign::Pad] Pad001
  BaseFeature = -> Pad
  Direction = (0,0,1)
  Length = 0.4
  Length2 = 10
  Profile = -> Sketch001
  ReferenceAxis = -> Sketch001 [N_Axis]
  Reversed = true
  Type = 0
FEATURE [PartDesign::LinearPattern] LinearPattern
  BaseFeature = -> Pad001
  Direction = -> Sketch001 [H_Axis]
  Length = 12
  Occurrences = 2
  Originals = -> [Pad001]
FEATURE [Sketcher::SketchObject] Sketch002
  FullyConstrained = true
  MapMode = 5
  Placement = pos=(0,0,0) rot=(1,0,0;3.14159rad)
  sketch-geometry (10):
    g0: ArcOfCircle CenterX=-5.15 CenterY=5.5 CenterZ=0 NormalX=0 NormalY=0 NormalZ=1 AngleXU=0 Radius=0.5 StartAngle=1.5708 EndAngle=3.14159
    g1: LineSegment StartX=-5.15 StartY=6 StartZ=0 EndX=1.85 EndY=6 EndZ=0
    g2: ArcOfCircle CenterX=1.85 CenterY=5.5 CenterZ=0 NormalX=0 NormalY=0 NormalZ=1 AngleXU=0 Radius=0.5 StartAngle=8e-16 EndAngle=1.5708
    g3: LineSegment StartX=2.35 StartY=5.5 StartZ=0 EndX=2.35 EndY=4.5 EndZ=0
    g4: ArcOfCircle CenterX=1.85 CenterY=4.5 CenterZ=0 NormalX=0 NormalY=0 NormalZ=1 AngleXU=0 Radius=0.5 StartAngle=4.71239 EndAngle=6.28319
    g5: LineSegment StartX=1.85 StartY=4 StartZ=0 EndX=-5.15 EndY=4 EndZ=0
    g6: ArcOfCircle CenterX=-5.15 CenterY=4.5 CenterZ=0 NormalX=0 NormalY=0 NormalZ=1 AngleXU=0 Radius=0.5 StartAngle=3.14159 EndAngle=4.71239
    g7: LineSegment StartX=-5.65 StartY=4.5 StartZ=0 EndX=-5.65 EndY=5.5 EndZ=0
    g8: GeomPoint X=-5.65 Y=6 Z=0
    g9: GeomPoint X=2.35 Y=4 Z=0
  constraints (24):
    c: Tangent(g0,g1) = 1.5708
    c: Tangent(g1,g2) = 1.5708
    c: Tangent(g2,g3) = 1.5708
    c: Tangent(g3,g4) = 1.5708
    c: Tangent(g4,g5) = 1.5708
    c: Tangent(g5,g6) = 1.5708
    c: Tangent(g6,g7) = 1.5708
    c: Tangent(g7,g0) = 1.5708
    c: Horizontal(g1)
    c: Horizontal(g5)
    c: Vertical(g3)
    c: Vertical(g7)
    c: Equal(g0,g2)
    c: Equal(g2,g4)
    c: Equal(g4,g6)
    c: PointOnObject(g8,g1)
    c: PointOnObject(g8,g7)
    c: PointOnObject(g9,g3)
    c: PointOnObject(g9,g5)
    c: Radius(g2) = 0.5
    c: DistanceY(g4,g1) = 2
    c: DistanceX(g1,g1) = 7
    c: DistanceX(g-1,g1) = 1.85
    c: DistanceY(g-1,g4) = 4
FEATURE [PartDesign::Pad] Pad002
  BaseFeature = -> LinearPattern
  Direction = (0,0,-1)
  Length = 0.4
  Length2 = 10
  Profile = -> Sketch002
  ReferenceAxis = -> Sketch002 [N_Axis]
  Type = 0
FEATURE [PartDesign::Body] Body  label="ShiftyStamp"
  Group = -> [Sketch,Pad,Sketch001,Pad001,LinearPattern,Sketch002,Pad002]
  Origin = -> Origin
  Tip = -> Pad002
FEATURE [Part::Refine] Body001  label="ShiftyStampR"
  Source = -> Body
COMPONENT P7 — recipe-attached ("MXCutoutR", a linked part whose construction recipe lives in a companion FreeCAD document of the same project; that document's serialized recipe follows).
Construction recipe (the companion document, serialized — sketch geometry with constraints, then the solid features built on it; lengths are millimeters unless a unit is written):

FCSTD DOCUMENT  (FreeCAD 0.21R33668 +26 (Git))
Label: MXCutout
License: All rights reserved
LicenseURL: http://en.wikipedia.org/wiki/All_rights_reserved
objects: Sketcher::SketchObject×3, PartDesign::Pad×3, PartDesign::Mirrored×1, PartDesign::Fillet×1, PartDesign::Body×1, Part::Refine×1
note: 14 computed .brp shape members not serialized (recipe doc carries the construction recipe); baked Part::Feature solids carry a one-line shape summary decoded from their .brp

FEATURE [Sketcher::SketchObject] Sketch
  FullyConstrained = true
  MapMode = 5
  Support = -> [XY_Plane]
  sketch-geometry (4):
    g0: LineSegment StartX=-7 StartY=7 StartZ=0 EndX=7 EndY=7 EndZ=0
    g1: LineSegment StartX=7 StartY=7 StartZ=0 EndX=7 EndY=-7 EndZ=0
    g2: LineSegment StartX=7 StartY=-7 StartZ=0 EndX=-7 EndY=-7 EndZ=0
    g3: LineSegment StartX=-7 StartY=-7 StartZ=0 EndX=-7 EndY=7 EndZ=0
  constraints (11):
    c: Coincident(g0,g1)
    c: Coincident(g1,g2)
    c: Coincident(g2,g3)
    c: Coincident(g3,g0)
    c: Horizontal(g0)
    c: Horizontal(g2)
    c: Vertical(g1)
    c: Vertical(g3)
    c: Symmetric(g0,g1,g-1)
    c: Equal(g3,g0)
    c: DistanceX(g0,g0) = 14
FEATURE [PartDesign::Pad] Pad
  Direction = (0,0,1)
  Length = 25
  Length2 = 10
  Profile = -> Sketch
  ReferenceAxis = -> Sketch [N_Axis]
  Reversed = true
  Type = 0
FEATURE [Sketcher::SketchObject] Sketch001
  ExternalGeometry = -> [Pad]
  FullyConstrained = true
  MapMode = 5
  Placement = pos=(0,7,0) rot=(0,0.707107,0.707107;3.14159rad)
  Support = -> [Pad]
  sketch-geometry (5):
    g0: LineSegment StartX=2.5 StartY=-25 StartZ=0 EndX=-2.5 EndY=-25 EndZ=0
    g1: LineSegment StartX=-2.5 StartY=-25 StartZ=0 EndX=-2.5 EndY=-1.4 EndZ=0
    g2: LineSegment StartX=-2.5 StartY=-1.4 StartZ=0 EndX=0 EndY=-1.4 EndZ=0
    g3: LineSegment StartX=0 StartY=-1.4 StartZ=0 EndX=2.5 EndY=-1.4 EndZ=0
    g4: LineSegment StartX=2.5 StartY=-25 StartZ=0 EndX=2.5 EndY=-1.4 EndZ=0
  constraints (15):
    c: Coincident(g0,g1)
    c: Horizontal(g0)
    c: DistanceX(g0,g0) = 5
    c: Coincident(g2,g1)
    c: Equal(g3,g2)
    c: Coincident(g3,g2)
    c: Vertical(g1)
    c: Coincident(g4,g0)
    c: Coincident(g4,g3)
    c: Vertical(g4)
    c: Horizontal(g2)
    c: Horizontal(g3)
    c: DistanceY(g3,g-1) = 1.4
    c: Horizontal(g0,g-3)
    c: Vertical(g2,g-1)
FEATURE [PartDesign::Pad] Pad001
  BaseFeature = -> Pad
  Direction = (0,1,-2e-16)
  Length = 0.5
  Length2 = 10
  Profile = -> Sketch001
  ReferenceAxis = -> Sketch001 [N_Axis]
  Type = 0
FEATURE [PartDesign::Mirrored] Mirrored
  BaseFeature = -> Pad001
  MirrorPlane = -> XZ_Plane
  Originals = -> [Pad001]
FEATURE [Sketcher::SketchObject] Sketch002
  ExternalGeometry = -> [Mirrored]
  FullyConstrained = true
  MapMode = 5
  Support = -> [Mirrored]
  sketch-geometry (4):
    g0: LineSegment StartX=-7 StartY=7 StartZ=0 EndX=7 EndY=7 EndZ=0
    g1: LineSegment StartX=7 StartY=7 StartZ=0 EndX=7 EndY=-7 EndZ=0
    g2: LineSegment StartX=7 StartY=-7 StartZ=0 EndX=-7 EndY=-7 EndZ=0
    g3: LineSegment StartX=-7 StartY=-7 StartZ=0 EndX=-7 EndY=7 EndZ=0
  constraints (10):
    c: Coincident(g0,g1)
    c: Coincident(g1,g2)
    c: Coincident(g2,g3)
    c: Coincident(g3,g0)
    c: Horizontal(g0)
    c: Horizontal(g2)
    c: Vertical(g1)
    c: Vertical(g3)
    c: Coincident(g0,g-3)
    c: Coincident(g1,g-4)
FEATURE [PartDesign::Pad] Pad002
  BaseFeature = -> Mirrored
  Direction = (0,0,1)
  Length = 10
  Length2 = 10
  Profile = -> Sketch002
  ReferenceAxis = -> Sketch002 [N_Axis]
  Refine = true
  Type = 0
FEATURE [PartDesign::Fillet] Fillet
  Base = -> Pad002 [Edge14,Edge16,Edge20,Edge36]
  BaseFeature = -> Pad002
  Radius = 0.5
  SupportTransform = false
  UseAllEdges = false
FEATURE [PartDesign::Body] Body  label="MXCutout"
  Group = -> [Sketch,Pad,Sketch001,Pad001,Mirrored,Sketch002,Pad002,Fillet]
  Origin = -> Origin
  Tip = -> Pad002
FEATURE [Part::Refine] Body001  label="MXCutoutR"
  Source = -> Fillet
PROVENANCE & LICENSES
A FreeCAD (.FCStd) document from a public repository crawl; recipes are the document's own serialized feature recipes (and, for linked parts, companion documents' recipes).
License: mit.
